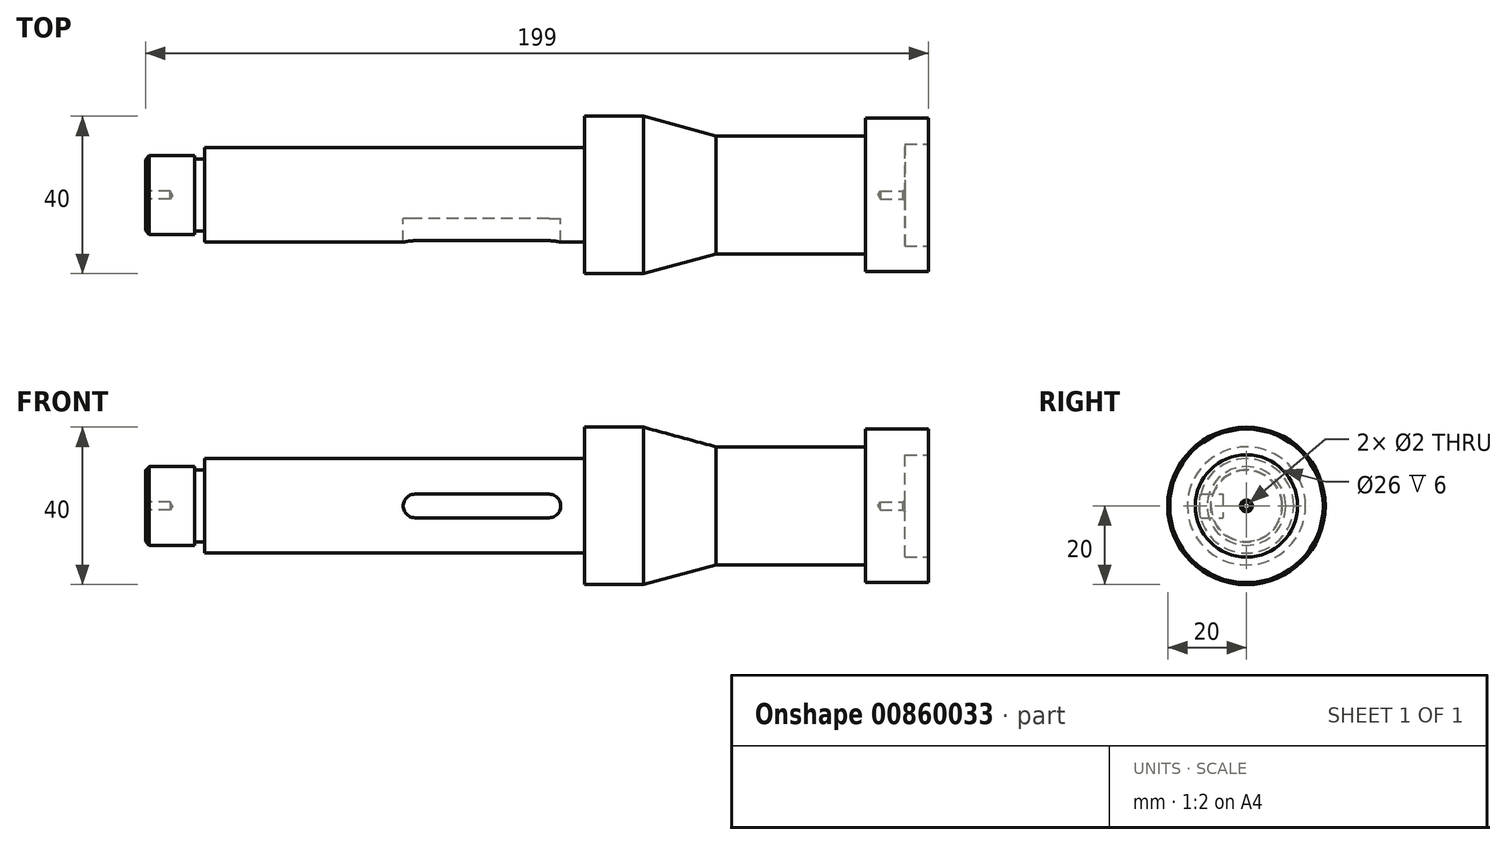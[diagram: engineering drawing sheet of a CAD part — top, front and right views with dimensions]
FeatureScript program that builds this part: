
annotation { "Feature Type Name" : "Feature", "Feature Type Description" : "" }
export const myFeature = defineFeature(function(context is Context, id is Id, definition is map)
    precondition{}
    {
        {
            var Q0;
            Q0=qCreatedBy(makeId("Front.planeOp"),FACE);
            var sketch = newSketch(context, id + "F0", { "sketchPlane" : qUnion([Q0])});
            skLineSegment(sketch, "E0", {"start": v(0, 9) * mm, "end": v(1, 10) * mm});
            skLineSegment(sketch, "E1", {"start": v(1, 10) * mm, "end": v(12.5, 10) * mm});
            skLineSegment(sketch, "E2", {"start": v(15, 12) * mm, "end": v(111.5, 12) * mm});
            skLineSegment(sketch, "E3", {"start": v(111.5, 12) * mm, "end": v(111.5, 20) * mm});
            skLineSegment(sketch, "E4", {"start": v(111.5, 20) * mm, "end": v(126.5, 20) * mm});
            skLineSegment(sketch, "E5", {"start": v(126.5, 20) * mm, "end": v(145, 15) * mm});
            skLineSegment(sketch, "E6", {"start": v(145, 15) * mm, "end": v(183, 15) * mm});
            skLineSegment(sketch, "E7", {"start": v(183, 15) * mm, "end": v(183, 0) * mm});
            skLineSegment(sketch, "E8", {"start": v(183, 0) * mm, "end": v(0, 0) * mm});
            skLineSegment(sketch, "E9", {"start": v(0, 9) * mm, "end": v(0, 0) * mm});
            skLineSegment(sketch, "E10", {"start": v(0, 0) * mm, "end": v(210.6, 0) * mm, "construction": true});
            skLineSegment(sketch, "E11", {"start": v(183, 15) * mm, "end": v(183, 19.5) * mm});
            skLineSegment(sketch, "E12", {"start": v(183, 19.5) * mm, "end": v(199, 19.5) * mm});
            skLineSegment(sketch, "E13", {"start": v(199, 19.5) * mm, "end": v(199, 0) * mm});
            skLineSegment(sketch, "E14", {"start": v(199, 0) * mm, "end": v(183, 0) * mm});
            skLineSegment(sketch, "E15", {"start": v(12.5, 9.15) * mm, "end": v(12.5, 10) * mm});
            skLineSegment(sketch, "E16", {"start": v(12.5, 9.15) * mm, "end": v(15, 9.15) * mm});
            skLineSegment(sketch, "E17", {"start": v(15, 9.15) * mm, "end": v(15, 12) * mm});
            skSolve(sketch);
        }
        {
            var Q0;
            Q0=qSketchRegion(id+"F0",true);
            var Q1;
            Q1=sQuery(id+"F0.wireOp",EDGE,"E10");
            revolve(context, id + "F1", {"surfaceOperationType" : NewSurfaceOperationType.NEW, "entities" : qUnion([Q0]), "axis" : qUnion([Q1]), "revolveType" : RevolveType.FULL});
        }
        {
            var Q0;
            Q0=qCreatedBy(makeId("Front.planeOp"),FACE);
            var sketch = newSketch(context, id + "F2", { "sketchPlane" : qUnion([Q0])});
            skLineSegment(sketch, "E18.bottom", {"start": v(102.5, 3) * mm, "end": v(68.5, 3) * mm});
            skLineSegment(sketch, "E18.top", {"start": v(102.5, -3) * mm, "end": v(68.5, -3) * mm});
            skPoint(sketch, "E18.middle", {"position": v(85.5, 0) * mm});
            skArc(sketch, "E19", {"start": v(68.5, 3) * mm, "mid": v(65.5, 0) * mm, "end": v(68.5, -3) * mm});
            skArc(sketch, "E20", {"start": v(102.5, -3) * mm, "mid": v(105.5, 0) * mm, "end": v(102.5, 3) * mm});
            skSolve(sketch);
        }
        {
            var Q0;
            Q0=qSketchRegion(id+"F2",true);
            extrude(context, id + "F3", {"entities" : qUnion([Q0]), "operationType" : NewBodyOperationType.REMOVE, "depth" : 15.4 * mm, "offsetDistance" : 25 * mm, "hasSecondDirection" : true, "secondDirectionOppositeDirection" : false, "secondDirectionDepth" : 6 * mm});
        }
        {
            var Q0;
            Q0=makeQuery(id+"F1.opRevolve","SWEPT_FACE",FACE,{"disambiguationData":[OSD([sQuery(id+"F0.wireOp",EDGE,"E13")])]});
            var sketch = newSketch(context, id + "F4", { "sketchPlane" : qUnion([Q0])});
            skCircle(sketch, "E21", {"center": v(0, 0) * mm, "radius": 13 * mm});
            skSolve(sketch);
        }
        {
            var Q0;
            Q0=qSketchRegion(id+"F4",true);
            extrude(context, id + "F5", {"entities" : qUnion([Q0]), "operationType" : NewBodyOperationType.REMOVE, "oppositeDirection" : true, "depth" : 6 * mm, "offsetDistance" : 25 * mm});
        }
        {
            var Q0;
            Q0=makeQuery(id+"F5.boolean.opBoolean","COPY",FACE,{"derivedFrom":makeQuery(id+"F5.opExtrude","CAP_FACE",FACE,{"disambiguationData":[OSD([sQuery(id+"F4.wireOp",EDGE,"E21")])],"isStart":false})});
            var sketch = newSketch(context, id + "F6", { "sketchPlane" : qUnion([Q0])});
            skPoint(sketch, "E22", {"position": v(0, 0) * mm});
            skSolve(sketch);
        }
        {
            var Q0;
            Q0=makeQuery(id+"F1.opRevolve","SWEPT_FACE",FACE,{"disambiguationData":[OSD([sQuery(id+"F0.wireOp",EDGE,"E9")])]});
            var sketch = newSketch(context, id + "F7", { "sketchPlane" : qUnion([Q0])});
            skPoint(sketch, "E23", {"position": v(0, 0) * mm});
            skSolve(sketch);
        }
        {
            var Q0;
            Q0=sQuery(id+"F7.wireOp",VERTEX,"E23");
            var Q1;
            Q1=sQuery(id+"F6.wireOp",VERTEX,"E22");
            var Q2;
            Q2=makeQuery(id+"F1.opRevolve","SWEPT_BODY",BODY,{"disambiguationData":[OSD([sQuery(id+"F0.wireOp",EDGE,"E0"),sQuery(id+"F0.wireOp",EDGE,"E1"),sQuery(id+"F0.wireOp",EDGE,"q1DnfAn3-i5U3-hMPg-zu84-WXOgAar5tqTj"),sQuery(id+"F0.wireOp",EDGE,"E2"),sQuery(id+"F0.wireOp",EDGE,"E3"),sQuery(id+"F0.wireOp",EDGE,"E4"),sQuery(id+"F0.wireOp",EDGE,"E5"),sQuery(id+"F0.wireOp",EDGE,"E6"),sQuery(id+"F0.wireOp",EDGE,"E8"),sQuery(id+"F0.wireOp",EDGE,"E9"),sQuery(id+"F0.wireOp",EDGE,"E11"),sQuery(id+"F0.wireOp",EDGE,"E12"),sQuery(id+"F0.wireOp",EDGE,"E13"),sQuery(id+"F0.wireOp",EDGE,"E14")])]});
            hole(context, id + "F8", {"style" : HoleStyle.C_SINK, "endStyle" : HoleEndStyle.BLIND, "holeDiameter" : 2 * mm, "cSinkDiameter" : 3 * mm, "cSinkAngle" : 90 * degree, "majorDiameter" : 5 * mm, "holeDepth" : 6.3 * mm, "isTappedThrough" : true, "tappedDepth" : 3.9 * mm, "tapClearance" : 3, "locations" : qUnion([Q0, Q1]), "scope" : qUnion([Q2])});
        }
    });
